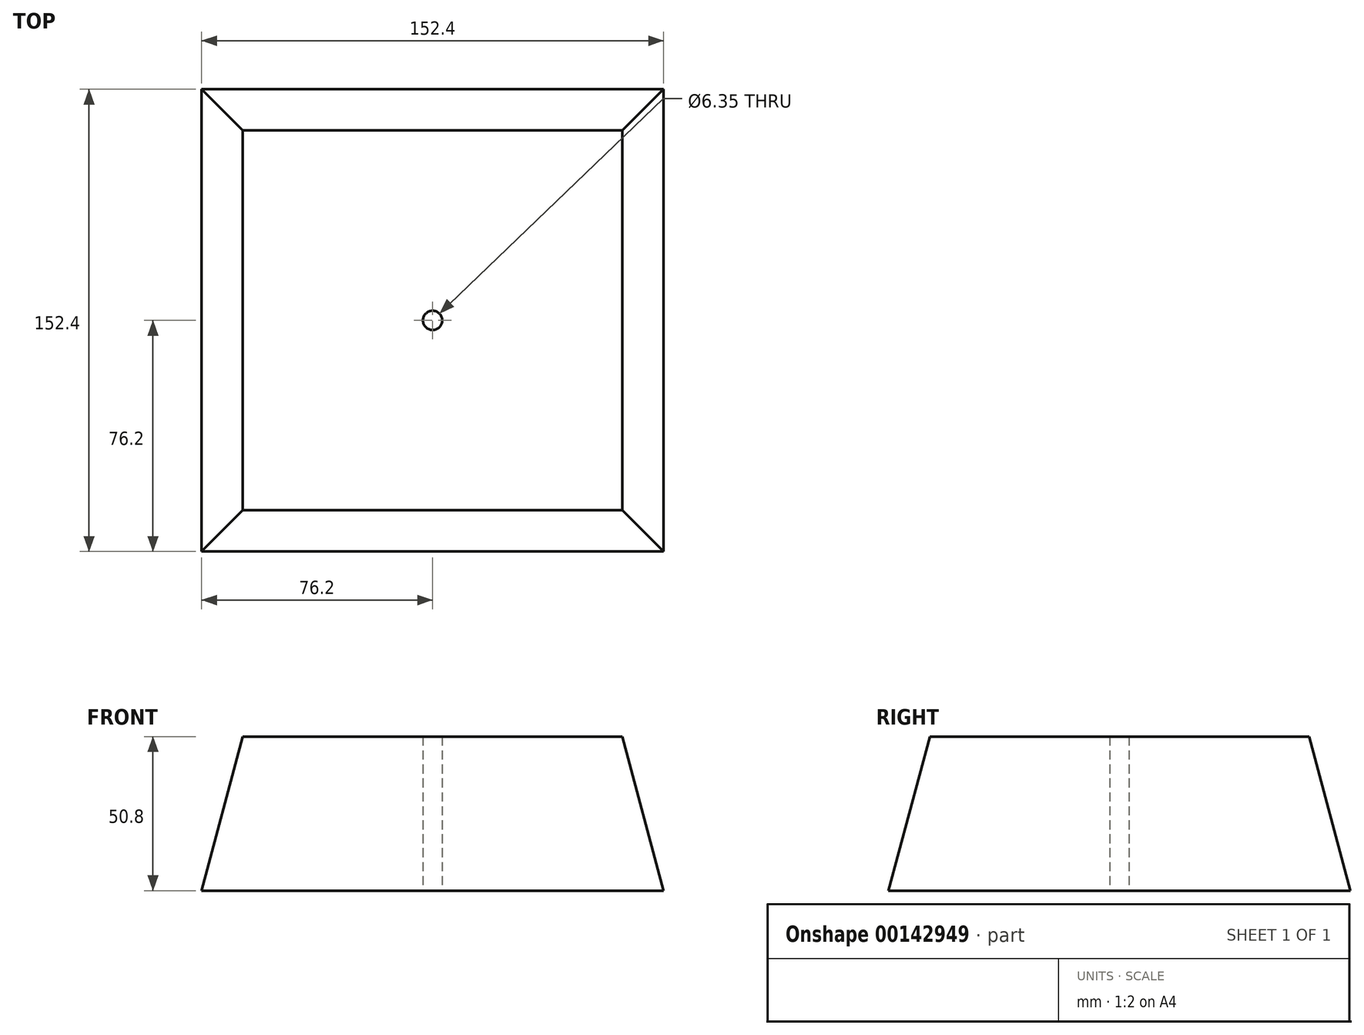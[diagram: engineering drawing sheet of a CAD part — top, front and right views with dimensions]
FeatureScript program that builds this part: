
annotation { "Feature Type Name" : "Feature", "Feature Type Description" : "" }
export const myFeature = defineFeature(function(context is Context, id is Id, definition is map)
    precondition{}
    {
        {
            var Q0;
            Q0=qCreatedBy(makeId("Top.planeOp"),FACE);
            var sketch = newSketch(context, id + "F0", { "sketchPlane" : qUnion([Q0])});
            skLineSegment(sketch, "E0.bottom", {"start": v(0, 0) * mm, "end": v(152.4, 0) * mm});
            skLineSegment(sketch, "E0.top", {"start": v(0, 152.4) * mm, "end": v(152.4, 152.4) * mm});
            skLineSegment(sketch, "E0.left", {"start": v(0, 0) * mm, "end": v(0, 152.4) * mm});
            skLineSegment(sketch, "E0.right", {"start": v(152.4, 0) * mm, "end": v(152.4, 152.4) * mm});
            skCircle(sketch, "E1", {"center": v(76.2, 76.2) * mm, "radius": 3.18 * mm});
            skPoint(sketch, "E1.centerSnap0", {"position": v(76.2, 0) * mm});
            skSolve(sketch);
        }
        {
            var Q0;
            Q0=makeQuery(id+"F0.imprint","IMPRINT",FACE,{"disambiguationData":[TD([[makeQuery(id+"F0.imprint","IMPRINT",EDGE,{"derivedFrom":sQuery(id+"F0.wireOp",EDGE,"V3q6LIwF-Q6QZ-MSZt-o16k-X46G89ltcXX3")}),1.0]])]});
            var Q1;
            Q1=makeQuery(id+"F0.imprint","IMPRINT",FACE,{"disambiguationData":[TD([[makeQuery(id+"F0.imprint","IMPRINT",EDGE,{"derivedFrom":sQuery(id+"F0.wireOp",EDGE,"E0.bottom")}),1.0]])]});
            extrude(context, id + "F1", {"entities" : qUnion([Q0, Q1]), "depth" : 50.8 * mm});
        }
        {
            var Q0;
            Q0=makeQuery(id+"F1.opExtrude","CAP_EDGE",EDGE,{"disambiguationData":[OSD([sQuery(id+"F0.wireOp",EDGE,"E0.left")])],"isStart":false});
            var Q1;
            Q1=makeQuery(id+"F1.opExtrude","CAP_EDGE",EDGE,{"disambiguationData":[OSD([sQuery(id+"F0.wireOp",EDGE,"E0.top")])],"isStart":false});
            var Q2;
            Q2=makeQuery(id+"F1.opExtrude","CAP_EDGE",EDGE,{"disambiguationData":[OSD([sQuery(id+"F0.wireOp",EDGE,"E0.right")])],"isStart":false});
            var Q3;
            Q3=makeQuery(id+"F1.opExtrude","CAP_EDGE",EDGE,{"disambiguationData":[OSD([sQuery(id+"F0.wireOp",EDGE,"E0.bottom")])],"isStart":false});
            chamfer(context, id + "F2", {"entities" : qUnion([Q0, Q1, Q2, Q3]), "chamferType" : ChamferType.OFFSET_ANGLE, "width" : 50.8 * mm, "oppositeDirection" : false, "angle" : 15 * degree, "tangentPropagation" : true});
        }
    });
